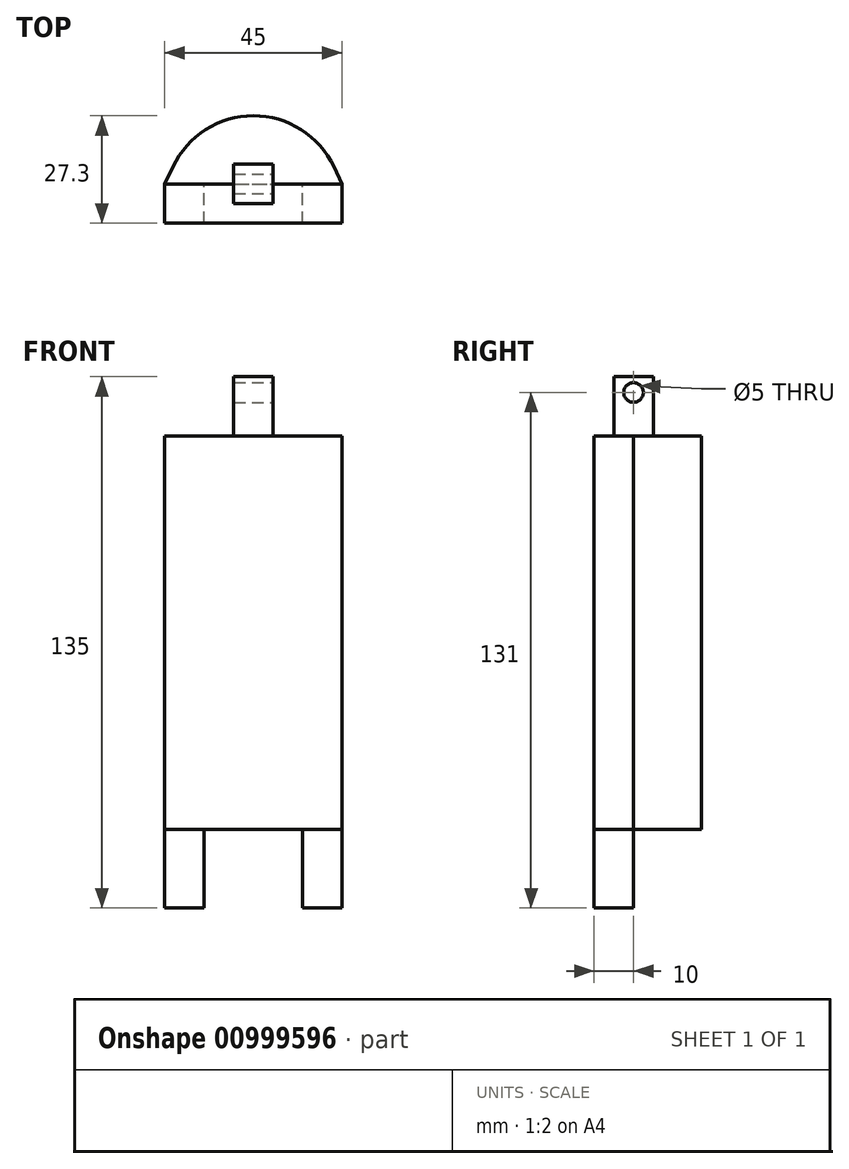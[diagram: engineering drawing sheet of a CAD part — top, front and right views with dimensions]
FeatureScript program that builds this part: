
annotation { "Feature Type Name" : "Feature", "Feature Type Description" : "" }
export const myFeature = defineFeature(function(context is Context, id is Id, definition is map)
    precondition{}
    {
        {
            var Q0;
            Q0=qCreatedBy(makeId("Top.planeOp"),FACE);
            var sketch = newSketch(context, id + "F0", { "sketchPlane" : qUnion([Q0])});
            skLineSegment(sketch, "E0.bottom", {"start": v(-22.5, 0) * mm, "end": v(-12.5, 0) * mm});
            skLineSegment(sketch, "E0.top", {"start": v(-22.5, 10) * mm, "end": v(-12.5, 10) * mm});
            skLineSegment(sketch, "E0.left", {"start": v(-22.5, 0) * mm, "end": v(-22.5, 10) * mm});
            skLineSegment(sketch, "E0.right", {"start": v(-12.5, 0) * mm, "end": v(-12.5, 10) * mm});
            skLineSegment(sketch, "E1.bottom", {"start": v(12.5, 0) * mm, "end": v(22.5, 0) * mm});
            skLineSegment(sketch, "E1.top", {"start": v(12.5, 10) * mm, "end": v(22.5, 10) * mm});
            skLineSegment(sketch, "E1.left", {"start": v(12.5, 0) * mm, "end": v(12.5, 10) * mm});
            skLineSegment(sketch, "E1.right", {"start": v(22.5, 0) * mm, "end": v(22.5, 10) * mm});
            skSolve(sketch);
        }
        {
            var Q0;
            Q0=makeQuery(id+"F0.imprint","IMPRINT",FACE,{"disambiguationData":[TD([[makeQuery(id+"F0.imprint","IMPRINT",EDGE,{"derivedFrom":sQuery(id+"F0.wireOp",EDGE,"E1.bottom")}),1.0]])]});
            var Q1;
            Q1=makeQuery(id+"F0.imprint","IMPRINT",FACE,{"disambiguationData":[TD([[makeQuery(id+"F0.imprint","IMPRINT",EDGE,{"derivedFrom":sQuery(id+"F0.wireOp",EDGE,"E0.bottom")}),1.0]])]});
            extrude(context, id + "F1", {"entities" : qUnion([Q0, Q1]), "depth" : 20 * mm, "offsetDistance" : 25 * mm});
        }
        {
            var Q0;
            Q0=makeQuery(id+"F1.opExtrude","CAP_FACE",FACE,{"disambiguationData":[OSD([sQuery(id+"F0.wireOp",EDGE,"E0.bottom"),sQuery(id+"F0.wireOp",EDGE,"E0.top"),sQuery(id+"F0.wireOp",EDGE,"E0.left"),sQuery(id+"F0.wireOp",EDGE,"E0.right")])],"isStart":false});
            var sketch = newSketch(context, id + "F2", { "sketchPlane" : qUnion([Q0])});
            skLineSegment(sketch, "E2", {"start": v(-22.5, 10) * mm, "end": v(22.5, 10) * mm});
            skLineSegment(sketch, "E3", {"start": v(-22.5, 10) * mm, "end": v(0, 57.6) * mm});
            skLineSegment(sketch, "E4", {"start": v(0, 57.6) * mm, "end": v(22.5, 10) * mm});
            skSolve(sketch);
        }
        {
            var Q0;
            {var subQ3=sQuery(id+"F2.wireOp",EDGE,"E3");Q0=makeQuery(id+"F2.imprint","IMPRINT",FACE,{"disambiguationData":[TD([[makeQuery(id+"F2.imprint","IMPRINT",EDGE,{"derivedFrom":subQ3}),-1.0]])]});}
            extrude(context, id + "F3", {"entities" : qUnion([Q0]), "depth" : 100 * mm, "offsetDistance" : 25 * mm});
        }
        {
            var Q0;
            Q0=makeQuery(id+"F3.opExtrude","SWEPT_EDGE",EDGE,{"disambiguationData":[OSD([sQuery(id+"F2.wireOp",EDGE,"E3"),sQuery(id+"F2.wireOp",EDGE,"E4")])]});
            fillet(context, id + "F4", {"entities" : qUnion([Q0]), "tangentPropagation" : true, "radius" : 22.6 * mm, "defaultsChanged" : true, "vertexSettings" : [], "allowEdgeOverflow" : false});
        }
        {
            var Q0;
            Q0=makeQuery(id+"F3.opExtrude","SWEPT_FACE",FACE,{"disambiguationData":[OSD([sQuery(id+"F2.wireOp",EDGE,"E2")])]});
            extrude(context, id + "F5", {"entities" : qUnion([Q0]), "depth" : 10 * mm, "offsetDistance" : 25 * mm});
        }
        {
            var Q0;
            {var subQ0=sQuery(id+"F2.wireOp",EDGE,"E2");Q0=makeQuery(id+"F5.opExtrude","SWEPT_FACE",FACE,{"disambiguationData":[OSD([subQ0]),TDD([makeQuery(id+"F3.opExtrude","CAP_EDGE",EDGE,{"disambiguationData":[OSD([subQ0])],"isStart":false})])]});}
            var sketch = newSketch(context, id + "F6", { "sketchPlane" : qUnion([Q0])});
            skLineSegment(sketch, "E5.bottom", {"start": v(5, 15) * mm, "end": v(-5, 15) * mm});
            skLineSegment(sketch, "E5.top", {"start": v(5, 5) * mm, "end": v(-5, 5) * mm});
            skLineSegment(sketch, "E5.left", {"start": v(5, 15) * mm, "end": v(5, 5) * mm});
            skLineSegment(sketch, "E5.right", {"start": v(-5, 15) * mm, "end": v(-5, 5) * mm});
            skPoint(sketch, "E5.middle", {"position": v(0, 10) * mm});
            skSolve(sketch);
        }
        {
            var Q0;
            {var subQ0=sQuery(id+"F6.wireOp",EDGE,"E5.bottom");Q0=makeQuery(id+"F6.imprint","IMPRINT",FACE,{"disambiguationData":[TD([[makeQuery(id+"F6.imprint","IMPRINT",EDGE,{"derivedFrom":subQ0}),1.0]])]});}
            var Q1;
            {var subQ0=sQuery(id+"F6.wireOp",EDGE,"E5.top");Q1=makeQuery(id+"F6.imprint","IMPRINT",FACE,{"disambiguationData":[TD([[makeQuery(id+"F6.imprint","IMPRINT",EDGE,{"derivedFrom":subQ0}),-1.0]])]});}
            extrude(context, id + "F7", {"entities" : qUnion([Q0, Q1]), "depth" : 15 * mm, "offsetDistance" : 25 * mm});
        }
        {
            var Q0;
            Q0=makeQuery(id+"F7.opExtrude","SWEPT_FACE",FACE,{"disambiguationData":[OSD([sQuery(id+"F6.wireOp",EDGE,"E5.left")])]});
            var sketch = newSketch(context, id + "F8", { "sketchPlane" : qUnion([Q0])});
            skCircle(sketch, "E6", {"center": v(10, 131) * mm, "radius": 2.5 * mm});
            skSolve(sketch);
        }
        {
            var Q0;
            Q0=makeQuery(id+"F8.imprint","IMPRINT",FACE,{"disambiguationData":[TD([[makeQuery(id+"F8.imprint","IMPRINT",EDGE,{"derivedFrom":sQuery(id+"F8.wireOp",EDGE,"E6")}),1.0]])]});
            extrude(context, id + "F9", {"entities" : qUnion([Q0]), "operationType" : NewBodyOperationType.REMOVE, "oppositeDirection" : true, "depth" : 25 * mm, "offsetDistance" : 25 * mm});
        }
    });
